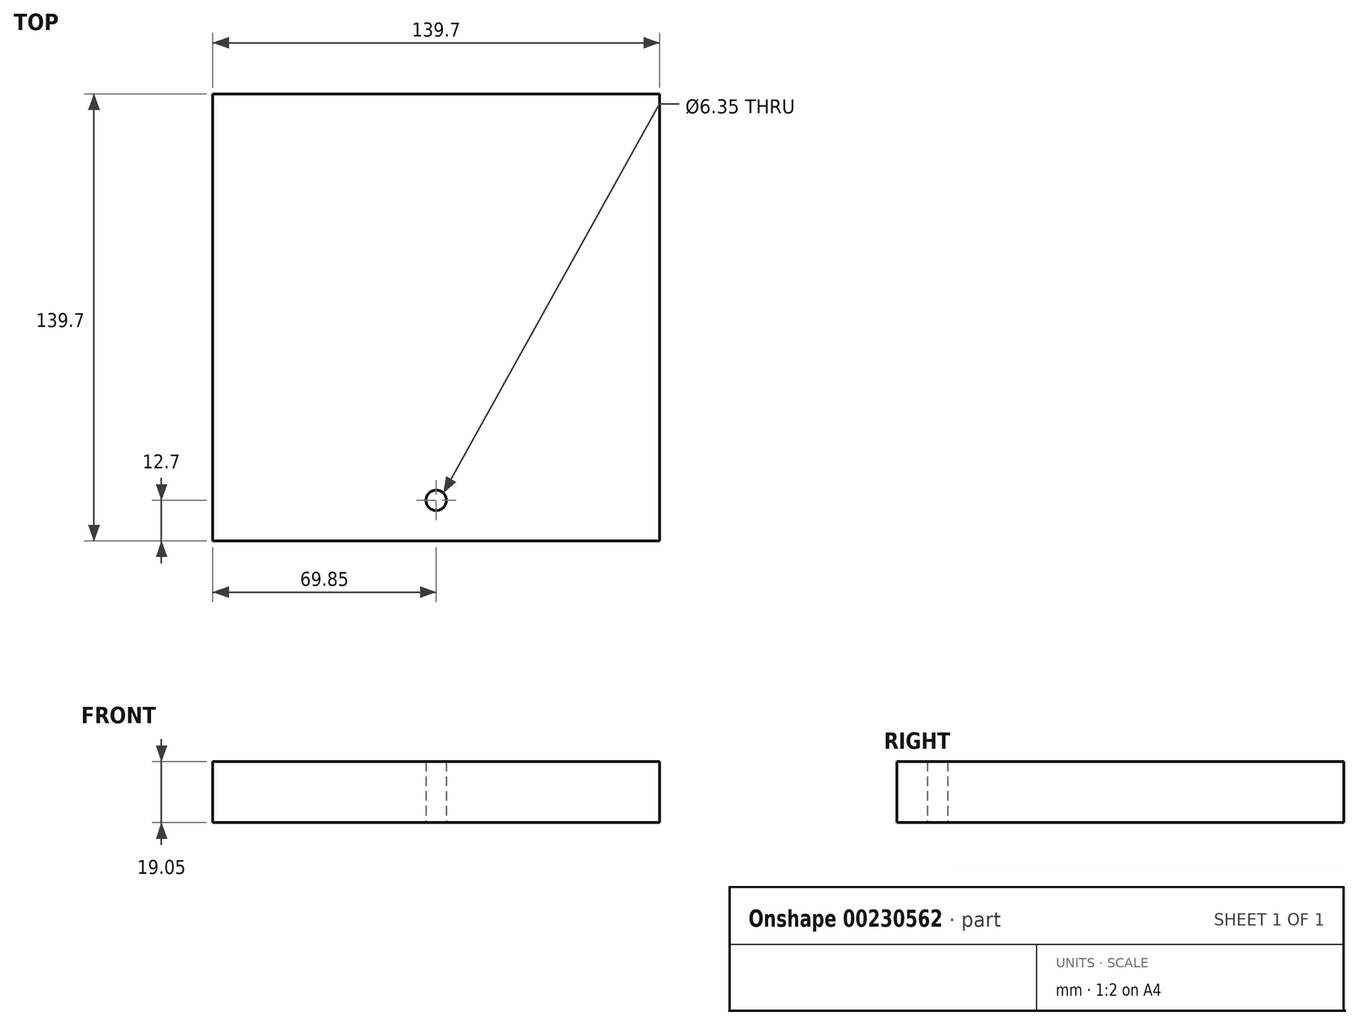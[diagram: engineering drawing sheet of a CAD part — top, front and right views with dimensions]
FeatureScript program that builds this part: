
annotation { "Feature Type Name" : "Feature", "Feature Type Description" : "" }
export const myFeature = defineFeature(function(context is Context, id is Id, definition is map)
    precondition{}
    {
        {
            var Q0;
            Q0=qCreatedBy(makeId("Top.planeOp"),FACE);
            var sketch = newSketch(context, id + "F0", { "sketchPlane" : qUnion([Q0])});
            skLineSegment(sketch, "E0.bottom", {"start": v(-69.85, 69.85) * mm, "end": v(69.85, 69.85) * mm});
            skLineSegment(sketch, "E0.top", {"start": v(-69.85, -69.85) * mm, "end": v(69.85, -69.85) * mm});
            skLineSegment(sketch, "E0.left", {"start": v(-69.85, 69.85) * mm, "end": v(-69.85, -69.85) * mm});
            skLineSegment(sketch, "E0.right", {"start": v(69.85, 69.85) * mm, "end": v(69.85, -69.85) * mm});
            skPoint(sketch, "E0.middle", {"position": v(0, 0) * mm});
            skLineSegment(sketch, "E1", {"start": v(0, -69.85) * mm, "end": v(0, -57.15) * mm});
            skPoint(sketch, "E1.endSnap0", {"position": v(0, -69.85) * mm});
            skCircle(sketch, "E2", {"center": v(0, -57.15) * mm, "radius": 3.18 * mm});
            skSolve(sketch);
        }
        {
            var Q0;
            Q0 = qSketchRegion(id + "F0", true);
            extrude(context, id + "F1", {"entities" : qUnion([Q0]), "depth" : 19.05 * mm});
        }
    });
